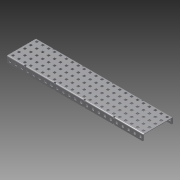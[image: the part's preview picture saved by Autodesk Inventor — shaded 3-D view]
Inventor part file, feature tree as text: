
AUTODESK INVENTOR PART (.ipt)
format: ipt  version: 2012 (Build 160160000, 160)  size: 1,831,936 bytes
history: native  units: in
note: dims shown in document units (in); Inventor stores cm internally (conversion verified against a paired STEP export)
features: other x1, imported_body x1, plane x1, split x1
ambient origin geometry x8: Origin, YZ Plane, XZ Plane, XY Plane, X Axis, Y Axis, Z Axis, Center Point
feature tree (4):
  parser-record x1  (decoder bookkeeping rows leaked as tree rows — omitted from the tree; the rows remain in map.json)
  imported_body  "Base1"
  plane  "Work Plane1"
  split  "Split1"
